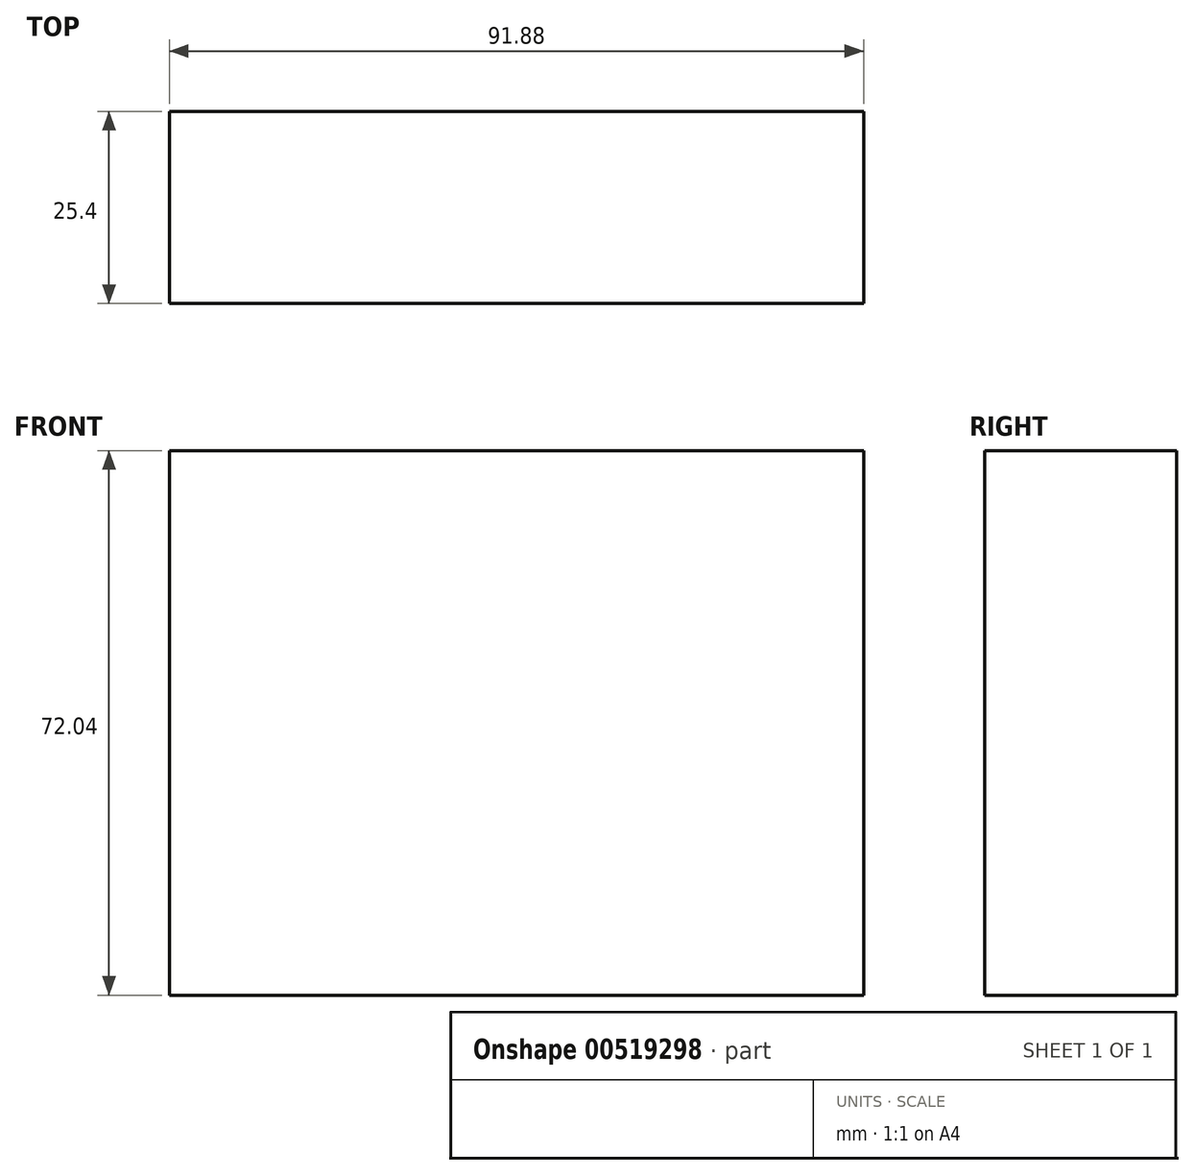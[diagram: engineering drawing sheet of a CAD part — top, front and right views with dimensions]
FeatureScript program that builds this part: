
annotation { "Feature Type Name" : "Feature", "Feature Type Description" : "" }
export const myFeature = defineFeature(function(context is Context, id is Id, definition is map)
    precondition{}
    {
        {
            var Q0;
            Q0=qCreatedBy(makeId("Front.planeOp"),FACE);
            var sketch = newSketch(context, id + "F0", { "sketchPlane" : qUnion([Q0])});
            skLineSegment(sketch, "E0.bottom", {"start": v(-46.4, 36.63) * mm, "end": v(45.48, 36.63) * mm});
            skLineSegment(sketch, "E0.top", {"start": v(-46.4, -35.41) * mm, "end": v(45.48, -35.41) * mm});
            skLineSegment(sketch, "E0.left", {"start": v(-46.4, 36.63) * mm, "end": v(-46.4, -35.41) * mm});
            skLineSegment(sketch, "E0.right", {"start": v(45.48, 36.63) * mm, "end": v(45.48, -35.41) * mm});
            skCircle(sketch, "E1", {"center": v(0, 0) * mm, "radius": 35.67 * mm});
            skSolve(sketch);
        }
        {
            var Q0;
            Q0=makeQuery(id+"F0.imprint","IMPRINT",FACE,{"disambiguationData":[TD([[makeQuery(id+"F0.imprint","IMPRINT",EDGE,{"derivedFrom":sQuery(id+"F0.wireOp",EDGE,"E0.bottom")}),-1.0]])]});
            var Q1;
            {var subQ0=sQuery(id+"F0.wireOp",EDGE,"E1");var subQ1=sQuery(id+"F0.wireOp",EDGE,"E0.top");var subQ2=makeQuery(id+"F0.imprint","INTERSECT",VERTEX,{"disambiguationData":[OD(0.0)],"derivedFrom":[subQ1,subQ0]});Q1=makeQuery(id+"F0.imprint","IMPRINT",FACE,{"disambiguationData":[TD([[makeQuery(id+"F0.imprint","IMPRINT",EDGE,{"disambiguationData":[TD([[subQ2,-1.0]])],"derivedFrom":subQ1}),1.0]])]});}
            extrude(context, id + "F1", {"entities" : qUnion([Q0, Q1]), "depth" : 25.4 * mm, "offsetDistance" : 25.4 * mm});
        }
    });
